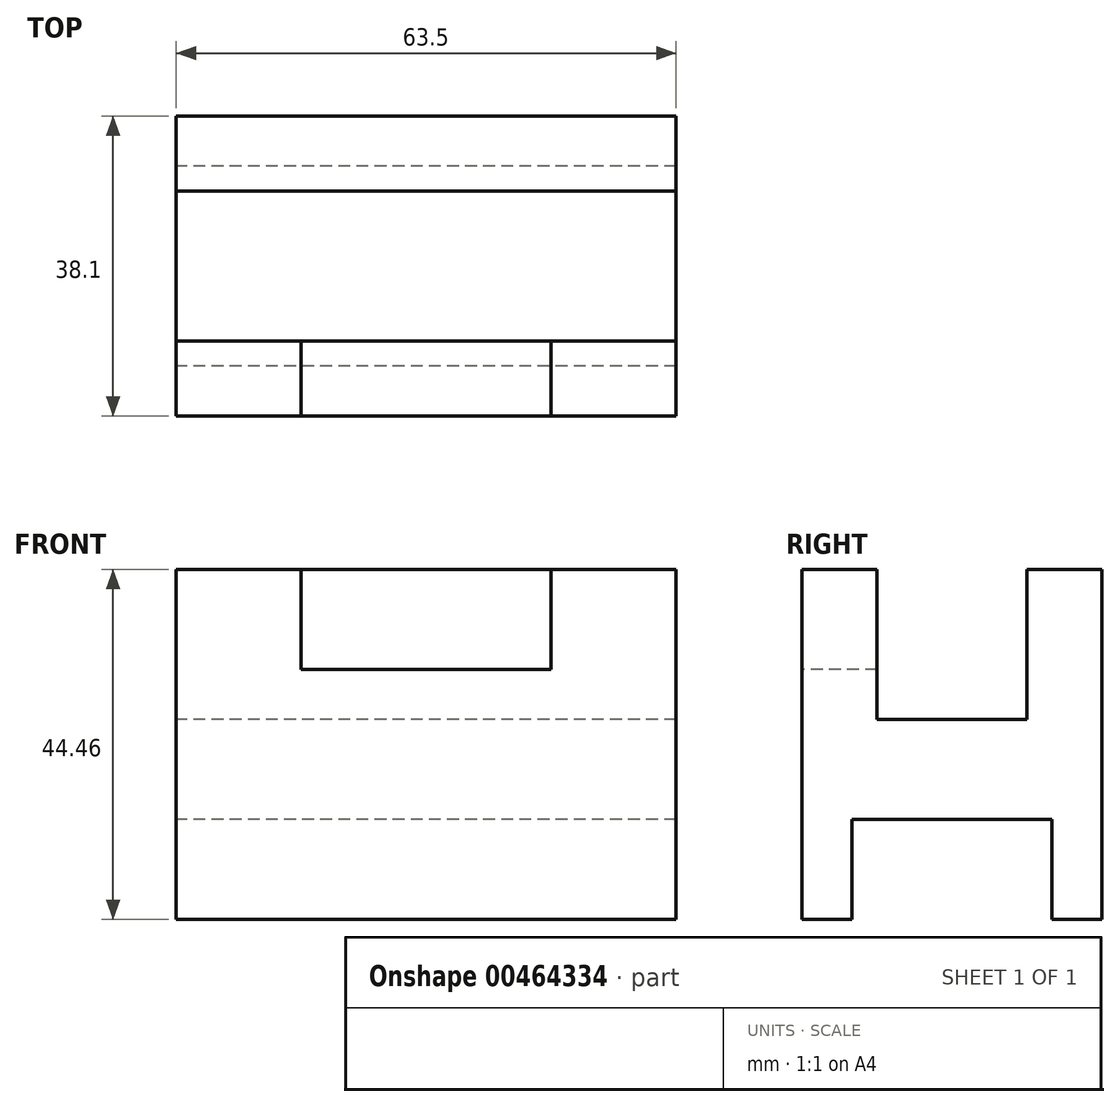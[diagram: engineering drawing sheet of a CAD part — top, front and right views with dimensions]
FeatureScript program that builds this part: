
annotation { "Feature Type Name" : "Feature", "Feature Type Description" : "" }
export const myFeature = defineFeature(function(context is Context, id is Id, definition is map)
    precondition{}
    {
        {
            var Q0;
            Q0=qCreatedBy(makeId("Front.planeOp"),FACE);
            var sketch = newSketch(context, id + "F0", { "sketchPlane" : qUnion([Q0])});
            skLineSegment(sketch, "E0.bottom", {"start": v(-31.75, 22.23) * mm, "end": v(31.75, 22.23) * mm});
            skLineSegment(sketch, "E0.top", {"start": v(-31.75, -22.23) * mm, "end": v(31.75, -22.23) * mm});
            skLineSegment(sketch, "E0.left", {"start": v(-31.75, 22.23) * mm, "end": v(-31.75, -22.23) * mm});
            skLineSegment(sketch, "E0.right", {"start": v(31.75, 22.23) * mm, "end": v(31.75, -22.23) * mm});
            skPoint(sketch, "E0.middle", {"position": v(0, 0) * mm});
            skSolve(sketch);
        }
        {
            var Q0;
            Q0=makeQuery(id+"F0.imprint","IMPRINT",FACE,{"disambiguationData":[TD([[makeQuery(id+"F0.imprint","IMPRINT",EDGE,{"derivedFrom":sQuery(id+"F0.wireOp",EDGE,"E0.bottom")}),-1.0]])]});
            extrude(context, id + "F1", {"entities" : qUnion([Q0]), "depth" : 38.1 * mm});
        }
        {
            var Q0;
            Q0=makeQuery(id+"F1.opExtrude","SWEPT_FACE",FACE,{"disambiguationData":[OSD([sQuery(id+"F0.wireOp",EDGE,"E0.bottom")])]});
            var sketch = newSketch(context, id + "F2", { "sketchPlane" : qUnion([Q0])});
            skLineSegment(sketch, "E1.bottom", {"start": v(31.75, -9.53) * mm, "end": v(-31.75, -9.53) * mm});
            skLineSegment(sketch, "E1.top", {"start": v(31.75, -28.58) * mm, "end": v(-31.75, -28.58) * mm});
            skLineSegment(sketch, "E1.left", {"start": v(31.75, -9.53) * mm, "end": v(31.75, -28.58) * mm});
            skLineSegment(sketch, "E1.right", {"start": v(-31.75, -9.53) * mm, "end": v(-31.75, -28.58) * mm});
            skPoint(sketch, "E1.middle", {"position": v(0, -19.05) * mm});
            skSolve(sketch);
        }
        {
            var Q0;
            Q0 = qSketchRegion(id + "F2", true);
            extrude(context, id + "F3", {"entities" : qUnion([Q0]), "operationType" : NewBodyOperationType.REMOVE, "oppositeDirection" : true, "depth" : 19.05 * mm});
        }
        {
            var Q0;
            Q0=makeQuery(id+"F1.opExtrude","SWEPT_FACE",FACE,{"disambiguationData":[OSD([sQuery(id+"F0.wireOp",EDGE,"E0.top")])]});
            var sketch = newSketch(context, id + "F4", { "sketchPlane" : qUnion([Q0])});
            skLineSegment(sketch, "E2.bottom", {"start": v(31.75, 6.35) * mm, "end": v(-31.75, 6.35) * mm});
            skLineSegment(sketch, "E2.top", {"start": v(31.75, 31.75) * mm, "end": v(-31.75, 31.75) * mm});
            skLineSegment(sketch, "E2.left", {"start": v(31.75, 6.35) * mm, "end": v(31.75, 31.75) * mm});
            skLineSegment(sketch, "E2.right", {"start": v(-31.75, 6.35) * mm, "end": v(-31.75, 31.75) * mm});
            skPoint(sketch, "E2.middle", {"position": v(0, 19.05) * mm});
            skSolve(sketch);
        }
        {
            var Q0;
            Q0 = qSketchRegion(id + "F4", true);
            extrude(context, id + "F5", {"entities" : qUnion([Q0]), "operationType" : NewBodyOperationType.REMOVE, "oppositeDirection" : true, "depth" : 12.7 * mm});
        }
        {
            var Q0;
            {var subQ2=sQuery(id+"F0.wireOp",EDGE,"E0.bottom");Q0=makeQuery(id+"F3.boolean.opBoolean","SPLIT",FACE,{"disambiguationData":[TD([makeQuery(id+"F3.opExtrude","SWEPT_FACE",FACE,{"disambiguationData":[OSD([sQuery(id+"F2.wireOp",EDGE,"E1.top")])]})])],"derivedFrom":makeQuery(id+"F1.opExtrude","SWEPT_FACE",FACE,{"disambiguationData":[OSD([subQ2])]})});}
            var sketch = newSketch(context, id + "F6", { "sketchPlane" : qUnion([Q0])});
            skLineSegment(sketch, "E3.bottom", {"start": v(-15.88, -28.58) * mm, "end": v(15.88, -28.58) * mm});
            skLineSegment(sketch, "E3.top", {"start": v(-15.88, -38.1) * mm, "end": v(15.88, -38.1) * mm});
            skLineSegment(sketch, "E3.left", {"start": v(-15.88, -28.58) * mm, "end": v(-15.88, -38.1) * mm});
            skLineSegment(sketch, "E3.right", {"start": v(15.88, -28.58) * mm, "end": v(15.88, -38.1) * mm});
            skPoint(sketch, "E3.middle", {"position": v(0, -33.34) * mm});
            skSolve(sketch);
        }
        {
            var Q0;
            Q0 = qSketchRegion(id + "F6", true);
            extrude(context, id + "F7", {"entities" : qUnion([Q0]), "operationType" : NewBodyOperationType.REMOVE, "oppositeDirection" : true, "depth" : 12.7 * mm});
        }
    });
